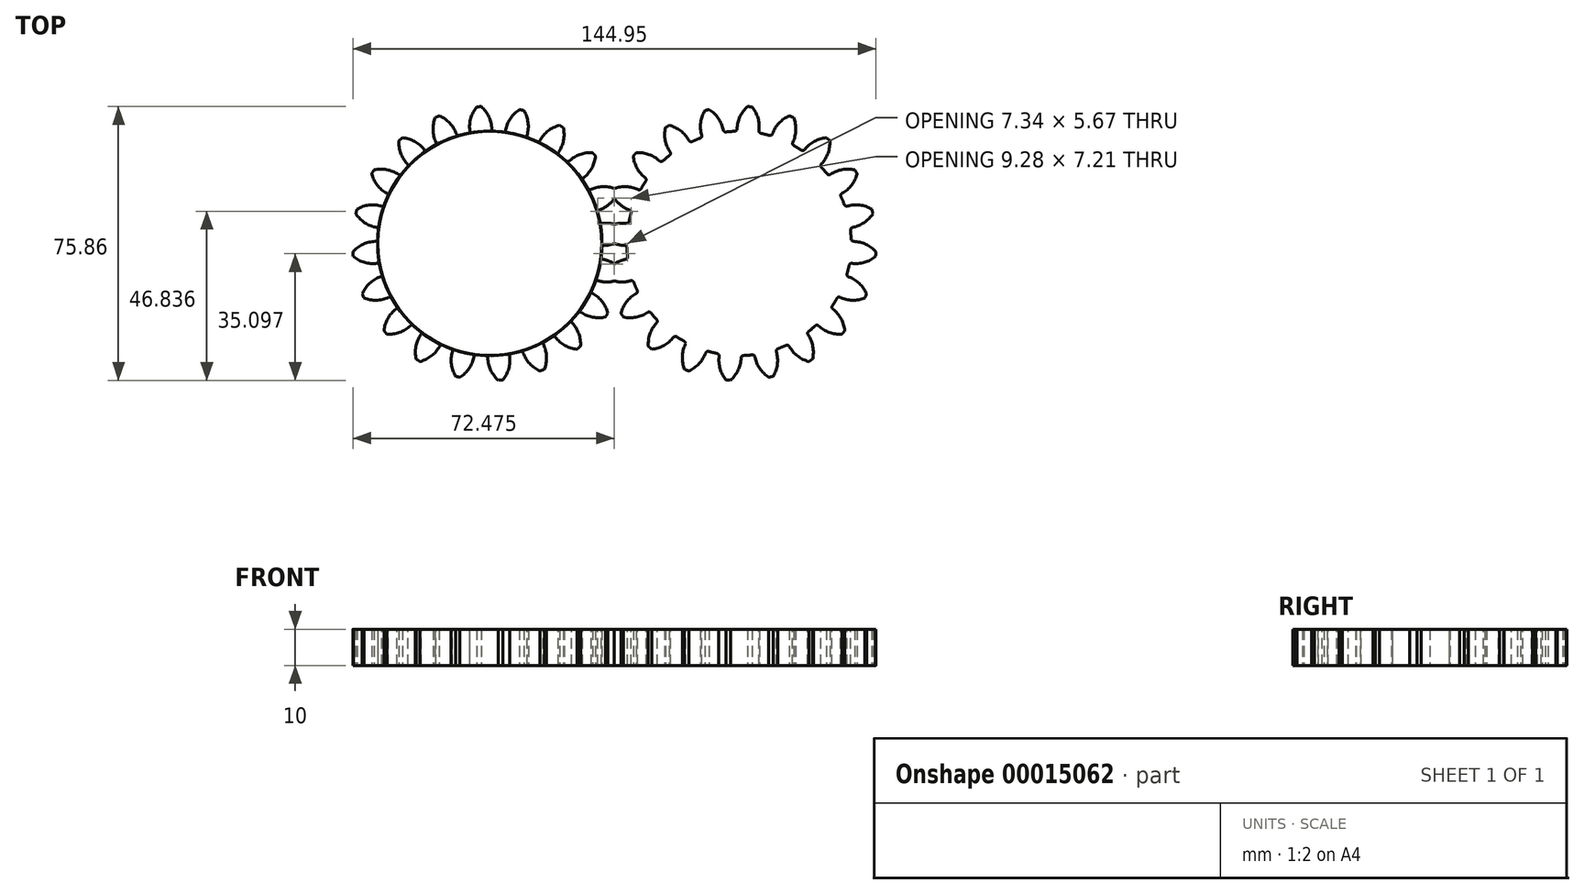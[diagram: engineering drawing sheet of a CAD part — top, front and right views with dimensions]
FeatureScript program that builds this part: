
annotation { "Feature Type Name" : "Feature", "Feature Type Description" : "" }
export const myFeature = defineFeature(function(context is Context, id is Id, definition is map)
    precondition{}
    {
        {
            var Q0;
            Q0=qCreatedBy(makeId("Top.planeOp"),FACE);
            var sketch = newSketch(context, id + "F0", { "sketchPlane" : qUnion([Q0])});
            skCircle(sketch, "E0", {"center": v(0, 0) * mm, "radius": 32.46 * mm, "construction": true});
            skCircle(sketch, "E1", {"center": v(69.1, 0) * mm, "radius": 31.09 * mm});
            skLineSegment(sketch, "E2", {"start": v(0, 0) * mm, "end": v(69.1, 0) * mm, "construction": true});
            skCircle(sketch, "E3", {"center": v(0, 0) * mm, "radius": 34.55 * mm, "construction": true});
            skCircle(sketch, "E4", {"center": v(0, 0) * mm, "radius": 31.09 * mm});
            skCircle(sketch, "E5", {"center": v(69.1, 0) * mm, "radius": 32.46 * mm, "construction": true});
            skCircle(sketch, "E6", {"center": v(69.1, 0) * mm, "radius": 34.55 * mm, "construction": true});
            skLineSegment(sketch, "E7", {"start": v(0, 0) * mm, "end": v(0, 47.04) * mm, "construction": true});
            skLineSegment(sketch, "E8", {"start": v(0, 0) * mm, "end": v(-3.7, 47.04) * mm, "construction": true});
            skLineSegment(sketch, "E9", {"start": v(69.1, 0) * mm, "end": v(69.1, 46.77) * mm, "construction": true});
            skLineSegment(sketch, "E10", {"start": v(69.1, 0) * mm, "end": v(72.77, 46.77) * mm, "construction": true});
            skLineSegment(sketch, "E11", {"start": v(0, 34.55) * mm, "end": v(-33, 34.54) * mm, "construction": true});
            skLineSegment(sketch, "E12", {"start": v(102.83, 34.55) * mm, "end": v(69.1, 34.55) * mm, "construction": true});
            skLineSegment(sketch, "E13", {"start": v(0, 34.55) * mm, "end": v(-33, 22.53) * mm, "construction": true});
            skLineSegment(sketch, "E14", {"start": v(102.83, 22.26) * mm, "end": v(69.1, 34.55) * mm, "construction": true});
            skCircle(sketch, "E15", {"center": v(0, 34.55) * mm, "radius": 8.63 * mm, "construction": true});
            skCircle(sketch, "E16", {"center": v(69.1, 34.55) * mm, "radius": 8.63 * mm, "construction": true});
            skArc(sketch, "E17", {"start": v(-2.35, 37.93) * mm, "mid": v(-16, 28.05) * mm, "end": v(0.57, 31.08) * mm, "construction": true});
            skArc(sketch, "E18", {"start": v(0.57, 31.08) * mm, "mid": v(-0.12, 34.84) * mm, "end": v(-2.35, 37.93) * mm});
            skArc(sketch, "E19", {"start": v(-2.98, 37.88) * mm, "mid": v(2.67, -37.9) * mm, "end": v(-2.35, 37.93) * mm, "construction": true});
            skArc(sketch, "E20", {"start": v(-2.35, 37.93) * mm, "mid": v(-2.67, 37.9) * mm, "end": v(-2.98, 37.88) * mm});
            skArc(sketch, "E21.0.MirrorCS", {"start": v(-3.6, 37.83) * mm, "mid": v(-3.3, 37.86) * mm, "end": v(-2.98, 37.88) * mm});
            skArc(sketch, "E22.0.MirrorCS", {"start": v(-5.42, 30.61) * mm, "mid": v(-5.33, 34.43) * mm, "end": v(-3.6, 37.83) * mm});
            skArc(sketch, "E23", {"start": v(71.44, 37.93) * mm, "mid": v(70.89, 37.39) * mm, "end": v(70.38, 36.8) * mm});
            skLineSegment(sketch, "E24", {"start": v(68.52, 31.08) * mm, "end": v(68.52, 31.08) * mm});
            skArc(sketch, "E25", {"start": v(68.52, 31.08) * mm, "mid": v(85.1, 28.05) * mm, "end": v(71.44, 37.93) * mm, "construction": true});
            skArc(sketch, "E26.0.MirrorCS", {"start": v(72.7, 37.83) * mm, "mid": v(74.42, 34.43) * mm, "end": v(74.51, 30.61) * mm});
            skArc(sketch, "E27", {"start": v(71.44, 37.93) * mm, "mid": v(66.1, -37.88) * mm, "end": v(72.7, 37.83) * mm, "construction": true});
            skArc(sketch, "E28", {"start": v(72.7, 37.83) * mm, "mid": v(72.07, 37.88) * mm, "end": v(71.44, 37.93) * mm});
            skArc(sketch, "E29", {"start": v(70.38, 36.8) * mm, "mid": v(68.94, 34.11) * mm, "end": v(68.52, 31.08) * mm});
            skSolve(sketch);
        }
        {
            var Q0;
            {var subQ0=sQuery(id+"F0.wireOp",EDGE,"E4");var subQ2=makeQuery(id+"F0.imprint","INTERSECT",VERTEX,{"derivedFrom":[subQ0,sQuery(id+"F0.wireOp",EDGE,"E18")]});Q0=makeQuery(id+"F0.imprint","IMPRINT",FACE,{"disambiguationData":[TD([[makeQuery(id+"F0.imprint","IMPRINT",EDGE,{"disambiguationData":[TD([[subQ2,-1.0]])],"derivedFrom":subQ0}),1.0]])]});}
            var Q1;
            {var subQ1=sQuery(id+"F0.wireOp",EDGE,"E18");Q1=makeQuery(id+"F0.imprint","IMPRINT",FACE,{"disambiguationData":[TD([[makeQuery(id+"F0.imprint","IMPRINT",EDGE,{"derivedFrom":subQ1}),1.0]])]});}
            var Q2;
            {var subQ0=sQuery(id+"F0.wireOp",EDGE,"E1");var subQ2=makeQuery(id+"F0.imprint","INTERSECT",VERTEX,{"derivedFrom":[subQ0,sQuery(id+"F0.wireOp",EDGE,"E26.0.MirrorCS")]});Q2=makeQuery(id+"F0.imprint","IMPRINT",FACE,{"disambiguationData":[TD([[makeQuery(id+"F0.imprint","IMPRINT",EDGE,{"disambiguationData":[TD([[subQ2,-1.0]])],"derivedFrom":subQ0}),1.0]])]});}
            var Q3;
            Q3=makeQuery(id+"F0.imprint","IMPRINT",FACE,{"disambiguationData":[TD([[makeQuery(id+"F0.imprint","IMPRINT",EDGE,{"derivedFrom":sQuery(id+"F0.wireOp",EDGE,"E23")}),1.0]])]});
            extrude(context, id + "F1", {"entities" : qUnion([Q0, Q1, Q2, Q3]), "depth" : 10 * mm});
        }
        {
            var Q0;
            Q0=makeQuery(id+"F1.opExtrude","SWEPT_EDGE",EDGE,{"disambiguationData":[OSD([sQuery(id+"F0.wireOp",EDGE,"E4"),sQuery(id+"F0.wireOp",EDGE,"E22.0.MirrorCS")])]});
            var Q1;
            Q1=makeQuery(id+"F1.opExtrude","SWEPT_EDGE",EDGE,{"disambiguationData":[OSD([sQuery(id+"F0.wireOp",EDGE,"E4"),sQuery(id+"F0.wireOp",EDGE,"E18")])]});
            fillet(context, id + "F2", {"entities" : qUnion([Q0, Q1]), "radius" : .69 * mm, "tangentPropagation" : true, "allowEdgeOverflow" : false});
        }
        {
            var Q0;
            Q0=makeQuery(id+"F1.opExtrude","SWEPT_EDGE",EDGE,{"disambiguationData":[OSD([sQuery(id+"F0.wireOp",EDGE,"E1"),sQuery(id+"F0.wireOp",EDGE,"E29")])]});
            var Q1;
            Q1=makeQuery(id+"F1.opExtrude","SWEPT_EDGE",EDGE,{"disambiguationData":[OSD([sQuery(id+"F0.wireOp",EDGE,"E1"),sQuery(id+"F0.wireOp",EDGE,"E26.0.MirrorCS")])]});
            fillet(context, id + "F3", {"entities" : qUnion([Q0, Q1]), "radius" : .69 * mm, "tangentPropagation" : true, "allowEdgeOverflow" : false});
        }
        {
            var Q0;
            Q0=makeQuery(id+"F1.opExtrude","SWEPT_BODY",BODY,{"disambiguationData":[OSD([sQuery(id+"F0.wireOp",EDGE,"E4"),sQuery(id+"F0.wireOp",EDGE,"E18"),sQuery(id+"F0.wireOp",EDGE,"E20"),sQuery(id+"F0.wireOp",EDGE,"E21.0.MirrorCS"),sQuery(id+"F0.wireOp",EDGE,"E22.0.MirrorCS")])]});
            var Q1;
            Q1=makeQuery(id+"F1.opExtrude","CAP_EDGE",EDGE,{"disambiguationData":[OSD([sQuery(id+"F0.wireOp",EDGE,"E4")])],"isStart":false});
            circularPattern(context, id + "F4", {"operationType" : NewBodyOperationType.ADD, "entities" : qUnion([Q0]), "axis" : qUnion([Q1]), "angle" : 360 * degree, "instanceCount" : round(20), "equalSpace" : true});
        }
        {
            var Q0;
            Q0=makeQuery(id+"F1.opExtrude","SWEPT_BODY",BODY,{"disambiguationData":[OSD([sQuery(id+"F0.wireOp",EDGE,"E1"),sQuery(id+"F0.wireOp",EDGE,"E23"),sQuery(id+"F0.wireOp",EDGE,"E26.0.MirrorCS"),sQuery(id+"F0.wireOp",EDGE,"E28"),sQuery(id+"F0.wireOp",EDGE,"E29")])]});
            var Q1;
            Q1=makeQuery(id+"F1.opExtrude","CAP_EDGE",EDGE,{"disambiguationData":[OSD([sQuery(id+"F0.wireOp",EDGE,"E1")])],"isStart":false});
            circularPattern(context, id + "F5", {"operationType" : NewBodyOperationType.ADD, "entities" : qUnion([Q0]), "axis" : qUnion([Q1]), "angle" : 360 * degree, "instanceCount" : round(20), "equalSpace" : true});
        }
    });
